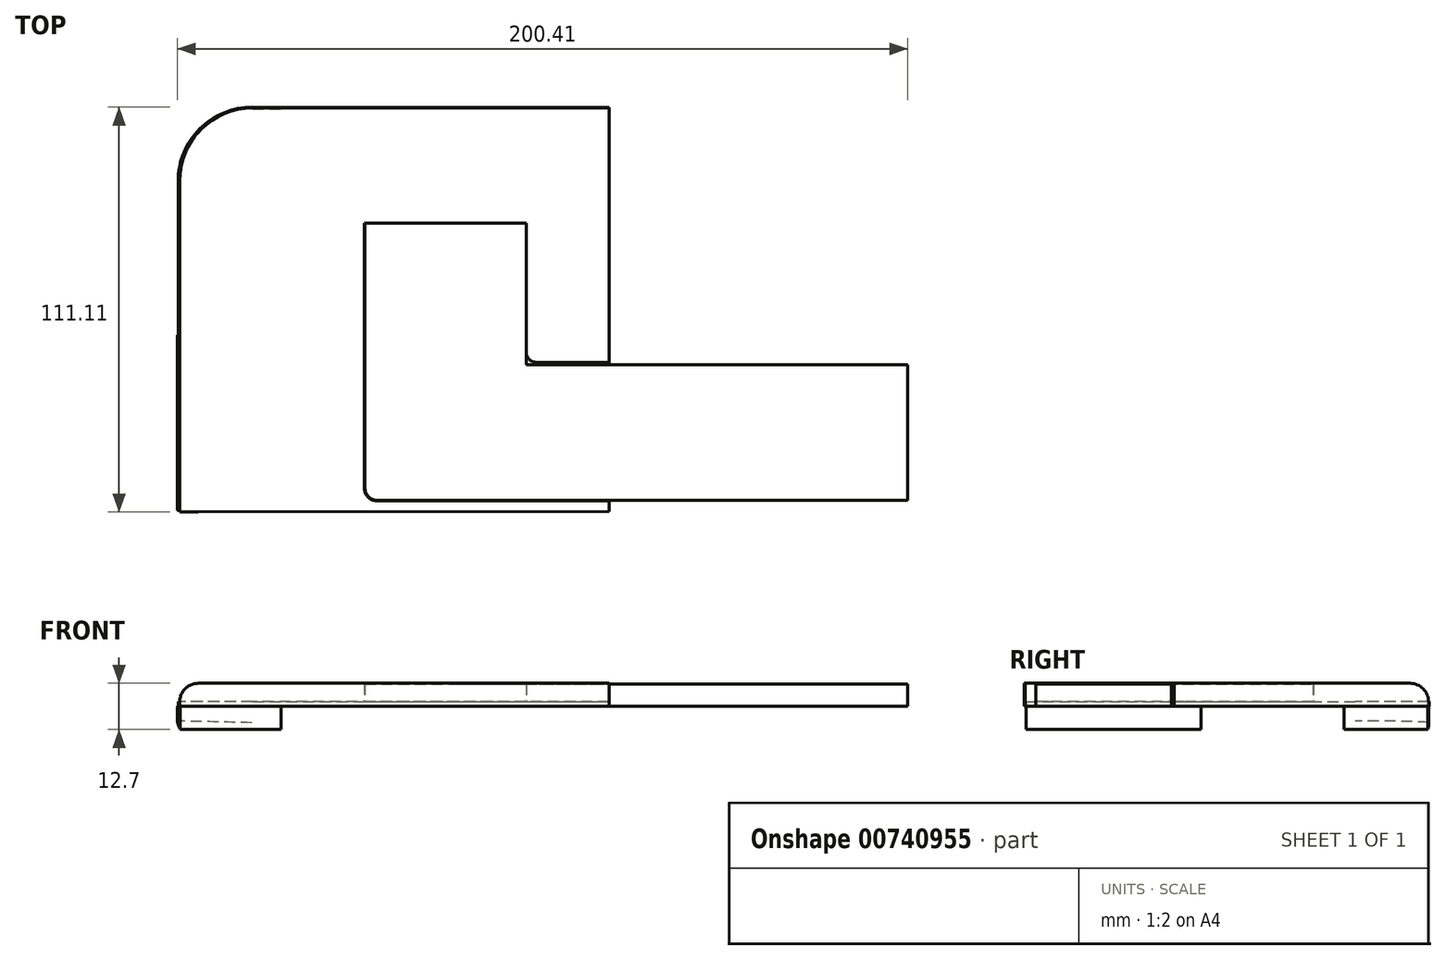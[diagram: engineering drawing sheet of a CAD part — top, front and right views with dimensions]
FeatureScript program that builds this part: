
annotation { "Feature Type Name" : "Feature", "Feature Type Description" : "" }
export const myFeature = defineFeature(function(context is Context, id is Id, definition is map)
    precondition{}
    {
        {
            var Q0;
            Q0=qCreatedBy(makeId("Top.planeOp"),FACE);
            var sketch = newSketch(context, id + "F0", { "sketchPlane" : qUnion([Q0])});
            skLineSegment(sketch, "E0", {"start": v(-57, -48.12) * mm, "end": v(-57, 42.23) * mm});
            skLineSegment(sketch, "E1", {"start": v(-57, -48.12) * mm, "end": v(61.23, -48.12) * mm});
            skLineSegment(sketch, "E2", {"start": v(61.23, -48.12) * mm, "end": v(61.23, 62.53) * mm});
            skLineSegment(sketch, "E3", {"start": v(61.23, 62.53) * mm, "end": v(-36.68, 62.55) * mm});
            skPoint(sketch, "E4.visualSharp", {"position": v(-57, 62.56) * mm});
            skArc(sketch, "E4.filletArc", {"start": v(-36.68, 62.55) * mm, "mid": v(-51.05, 56.6) * mm, "end": v(-57, 42.23) * mm});
            skSolve(sketch);
        }
        {
            var Q0;
            Q0=qSketchRegion(id+"F0",true);
            extrude(context, id + "F1", {"entities" : qUnion([Q0]), "depth" : 1.27 * mm, "offsetDistance" : 25.4 * mm});
        }
        {
            var Q0;
            Q0=qCreatedBy(makeId("Top.planeOp"),FACE);
            var sketch = newSketch(context, id + "F2", { "sketchPlane" : qUnion([Q0])});
            skLineSegment(sketch, "E5", {"start": v(-28.79, 62.5) * mm, "end": v(-36.74, 62.5) * mm});
            skLineSegment(sketch, "E6", {"start": v(-56.99, 42.26) * mm, "end": v(-56.99, 39.26) * mm});
            skPoint(sketch, "E7.visualSharp", {"position": v(-56.99, 62.5) * mm});
            skArc(sketch, "E7.filletArc", {"start": v(-36.74, 62.5) * mm, "mid": v(-51.06, 56.57) * mm, "end": v(-56.99, 42.26) * mm});
            skLineSegment(sketch, "E8", {"start": v(-56.99, 39.26) * mm, "end": v(-56.99, 42.26) * mm});
            skLineSegment(sketch, "E9", {"start": v(-56.99, 39.26) * mm, "end": v(-56.41, 39.26) * mm});
            skLineSegment(sketch, "E10", {"start": v(-56.41, 39.26) * mm, "end": v(-56.41, 42.26) * mm});
            skLineSegment(sketch, "E11", {"start": v(-36.53, 62.14) * mm, "end": v(-28.8, 62.14) * mm});
            skLineSegment(sketch, "E12", {"start": v(-28.8, 62.14) * mm, "end": v(-28.79, 62.5) * mm});
            skPoint(sketch, "E13.visualSharp", {"position": v(-56.41, 62.14) * mm});
            skArc(sketch, "E13.filletArc", {"start": v(-36.53, 62.14) * mm, "mid": v(-50.59, 56.32) * mm, "end": v(-56.41, 42.26) * mm});
            skLineSegment(sketch, "E14", {"start": v(-57.2, 0) * mm, "end": v(-57.2, -48.1) * mm});
            skLineSegment(sketch, "E15", {"start": v(-57.2, 0) * mm, "end": v(-56.4, 0) * mm});
            skLineSegment(sketch, "E16", {"start": v(-56.4, 0) * mm, "end": v(-56.4, -48.1) * mm});
            skLineSegment(sketch, "E17", {"start": v(-56.4, -48.1) * mm, "end": v(-57.2, -48.1) * mm});
            skSolve(sketch);
        }
        {
            var Q0;
            Q0=qSketchRegion(id+"F2",true);
            extrude(context, id + "F3", {"entities" : qUnion([Q0]), "operationType" : NewBodyOperationType.ADD, "depth" : -6.35 * mm, "offsetDistance" : 25.4 * mm});
        }
        {
            var Q0;
            Q0=qCreatedBy(makeId("Top.planeOp"),FACE);
            var sketch = newSketch(context, id + "F4", { "sketchPlane" : qUnion([Q0])});
            skLineSegment(sketch, "E18", {"start": v(61.23, -48.34) * mm, "end": v(61.23, -45.45) * mm});
            skLineSegment(sketch, "E19", {"start": v(61.23, -45.45) * mm, "end": v(-2.48, -45.45) * mm});
            skLineSegment(sketch, "E20", {"start": v(-5.89, -42.04) * mm, "end": v(-5.89, 30.78) * mm});
            skLineSegment(sketch, "E21", {"start": v(-5.89, 30.78) * mm, "end": v(38.56, 30.78) * mm});
            skLineSegment(sketch, "E22", {"start": v(38.56, 30.78) * mm, "end": v(38.56, -4.84) * mm});
            skLineSegment(sketch, "E23", {"start": v(41.17, -7.45) * mm, "end": v(61.31, -7.45) * mm});
            skLineSegment(sketch, "E24", {"start": v(61.31, -7.45) * mm, "end": v(61.31, 62.38) * mm});
            skLineSegment(sketch, "E25", {"start": v(61.31, 62.38) * mm, "end": v(-36.48, 62.38) * mm});
            skLineSegment(sketch, "E26", {"start": v(-56.57, 42.29) * mm, "end": v(-56.57, -48.56) * mm});
            skLineSegment(sketch, "E27", {"start": v(-56.57, -48.56) * mm, "end": v(61.23, -48.34) * mm});
            skPoint(sketch, "E28.visualSharp", {"position": v(-56.57, 62.38) * mm});
            skArc(sketch, "E28.filletArc", {"start": v(-36.48, 62.38) * mm, "mid": v(-50.69, 56.5) * mm, "end": v(-56.57, 42.29) * mm});
            skPoint(sketch, "E29.visualSharp", {"position": v(-5.89, -45.45) * mm});
            skArc(sketch, "E29.filletArc", {"start": v(-5.89, -42.04) * mm, "mid": v(-4.9, -44.45) * mm, "end": v(-2.48, -45.45) * mm});
            skPoint(sketch, "E30.visualSharp", {"position": v(38.56, -7.45) * mm});
            skArc(sketch, "E30.filletArc", {"start": v(38.56, -4.84) * mm, "mid": v(39.32, -6.68) * mm, "end": v(41.17, -7.45) * mm});
            skSolve(sketch);
        }
        {
            var Q0;
            Q0=makeQuery(id+"F4.imprint","IMPRINT",FACE,{"disambiguationData":[TD([[makeQuery(id+"F4.imprint","IMPRINT",EDGE,{"derivedFrom":sQuery(id+"F4.wireOp",EDGE,"E18")}),1.0]])]});
            var Q1;
            Q1=qSketchRegion(id+"F4",true);
            extrude(context, id + "F5", {"entities" : qUnion([Q0, Q1]), "operationType" : NewBodyOperationType.ADD, "depth" : 6.35 * mm, "offsetDistance" : 25.4 * mm});
        }
        {
            var Q0;
            Q0=makeQuery(id+"F5.opExtrude","CAP_EDGE",EDGE,{"disambiguationData":[OSD([sQuery(id+"F4.wireOp",EDGE,"E25")])],"isStart":false});
            fillet(context, id + "F6", {"entities" : qUnion([Q0]), "radius" : 5.08 * mm, "tangentPropagation" : true, "allowEdgeOverflow" : false});
        }
        {
            var Q0;
            Q0=makeQuery(id+"F3.opExtrude","CAP_EDGE",EDGE,{"disambiguationData":[OSD([sQuery(id+"F2.wireOp",EDGE,"E5")])],"isStart":false});
            fillet(context, id + "F7", {"entities" : qUnion([Q0]), "radius" : 5.08 * mm, "tangentPropagation" : true, "allowEdgeOverflow" : false});
        }
        {
            var Q0;
            Q0=makeQuery(id+"F3.opExtrude","CAP_EDGE",EDGE,{"disambiguationData":[OSD([sQuery(id+"F2.wireOp",EDGE,"E14")])],"isStart":false});
            fillet(context, id + "F8", {"entities" : qUnion([Q0]), "radius" : 5.08 * mm, "tangentPropagation" : true, "allowEdgeOverflow" : false});
        }
        {
            var Q0;
            Q0=qCreatedBy(makeId("Top.planeOp"),FACE);
            var sketch = newSketch(context, id + "F9", { "sketchPlane" : qUnion([Q0])});
            skLineSegment(sketch, "E31", {"start": v(-5.82, 30.72) * mm, "end": v(38.53, 30.77) * mm});
            skLineSegment(sketch, "E32", {"start": v(38.53, 30.77) * mm, "end": v(38.53, -8.13) * mm});
            skLineSegment(sketch, "E33", {"start": v(38.53, -8.13) * mm, "end": v(143.21, -8.13) * mm});
            skLineSegment(sketch, "E34", {"start": v(19.09, -45.35) * mm, "end": v(-2.23, -45.37) * mm});
            skLineSegment(sketch, "E35", {"start": v(-5.74, -41.87) * mm, "end": v(-5.82, 30.72) * mm});
            skLineSegment(sketch, "E36", {"start": v(19.09, -45.35) * mm, "end": v(143.21, -45.35) * mm});
            skLineSegment(sketch, "E37", {"start": v(143.21, -8.13) * mm, "end": v(143.21, -45.35) * mm});
            skPoint(sketch, "E38.visualSharp", {"position": v(-5.74, -45.38) * mm});
            skArc(sketch, "E38.filletArc", {"start": v(-5.74, -41.87) * mm, "mid": v(-4.71, -44.35) * mm, "end": v(-2.23, -45.37) * mm});
            skSolve(sketch);
        }
        {
            var Q0;
            Q0 = qSketchRegion(id + "F9", true);
            extrude(context, id + "F10", {"entities" : qUnion([Q0]), "operationType" : NewBodyOperationType.ADD, "depth" : 6.1 * mm, "offsetDistance" : 25.4 * mm});
        }
    });
